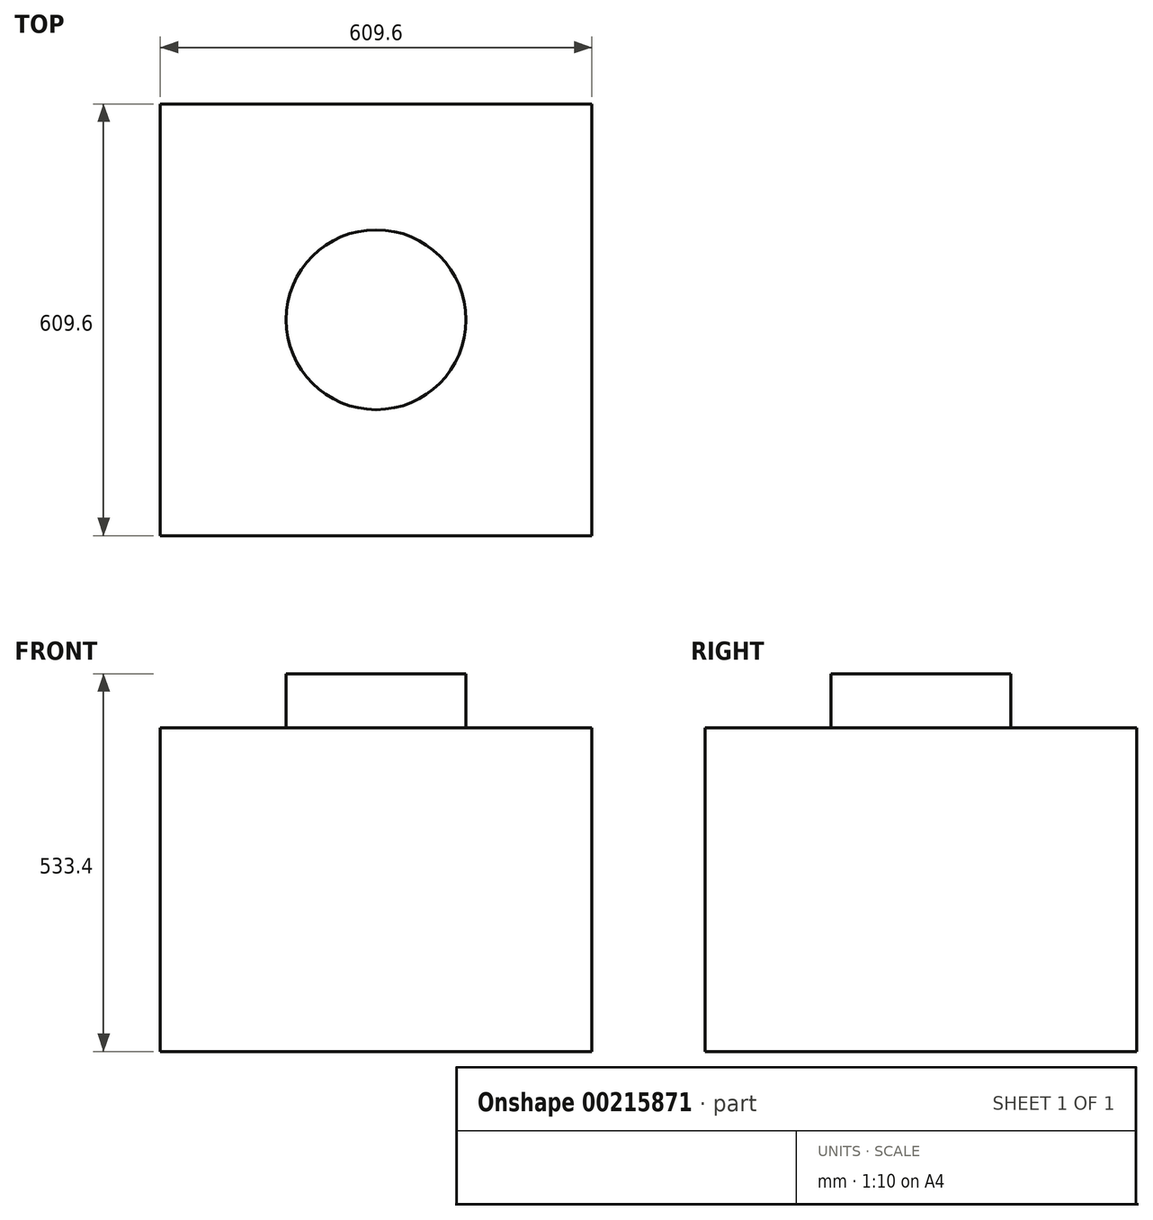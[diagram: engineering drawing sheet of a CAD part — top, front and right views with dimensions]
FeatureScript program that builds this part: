
annotation { "Feature Type Name" : "Feature", "Feature Type Description" : "" }
export const myFeature = defineFeature(function(context is Context, id is Id, definition is map)
    precondition{}
    {
        {
            var Q0;
            Q0=qCreatedBy(makeId("Top.planeOp"),FACE);
            var sketch = newSketch(context, id + "F0", { "sketchPlane" : qUnion([Q0])});
            skLineSegment(sketch, "E0.bottom", {"start": v(-304.8, 304.8) * mm, "end": v(304.8, 304.8) * mm});
            skLineSegment(sketch, "E0.top", {"start": v(-304.8, -304.8) * mm, "end": v(304.8, -304.8) * mm});
            skLineSegment(sketch, "E0.left", {"start": v(-304.8, 304.8) * mm, "end": v(-304.8, -304.8) * mm});
            skLineSegment(sketch, "E0.right", {"start": v(304.8, 304.8) * mm, "end": v(304.8, -304.8) * mm});
            skSolve(sketch);
        }
        {
            var Q0;
            Q0 = qSketchRegion(id + "F0", true);
            extrude(context, id + "F1", {"entities" : qUnion([Q0]), "oppositeDirection" : true, "depth" : 457.2 * mm});
        }
        {
            var Q0;
            Q0=makeQuery(id+"F1.opExtrude","CAP_FACE",FACE,{"disambiguationData":[OSD([sQuery(id+"F0.wireOp",EDGE,"E0.bottom"),sQuery(id+"F0.wireOp",EDGE,"E0.top"),sQuery(id+"F0.wireOp",EDGE,"E0.left"),sQuery(id+"F0.wireOp",EDGE,"E0.right")])],"isStart":true});
            var sketch = newSketch(context, id + "F2", { "sketchPlane" : qUnion([Q0])});
            skCircle(sketch, "E1", {"center": v(0, 0) * mm, "radius": 127 * mm});
            skSolve(sketch);
        }
        {
            var Q0;
            Q0 = qSketchRegion(id + "F2", true);
            extrude(context, id + "F3", {"entities" : qUnion([Q0]), "operationType" : NewBodyOperationType.ADD, "depth" : 76.2 * mm});
        }
    });
